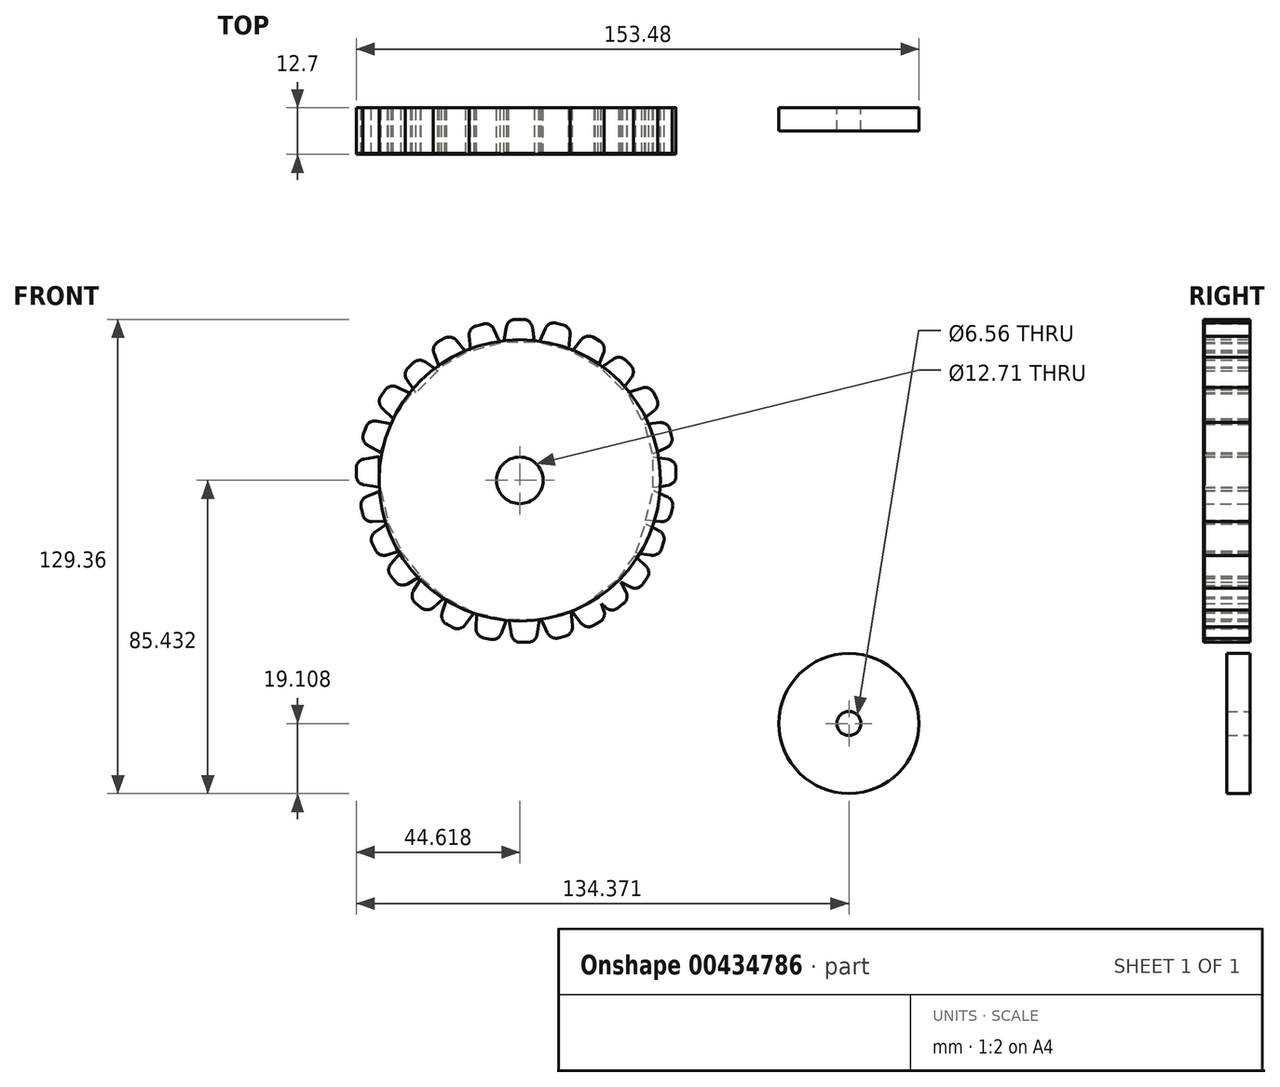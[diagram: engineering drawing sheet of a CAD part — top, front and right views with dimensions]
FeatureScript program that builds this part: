
annotation { "Feature Type Name" : "Feature", "Feature Type Description" : "" }
export const myFeature = defineFeature(function(context is Context, id is Id, definition is map)
    precondition{}
    {
        {
            var Q0;
            Q0=qCreatedBy(makeId("Front.planeOp"),FACE);
            var sketch = newSketch(context, id + "F0", { "sketchPlane" : qUnion([Q0])});
            skCircle(sketch, "E0", {"center": v(-43.7, 42.4) * mm, "radius": 38.36 * mm});
            skCircle(sketch, "E1", {"center": v(-43.7, 42.4) * mm, "radius": 6.36 * mm});
            skSolve(sketch);
        }
        {
            var Q0;
            Q0 = qSketchRegion(id + "F0", true);
            extrude(context, id + "F1", {"entities" : qUnion([Q0]), "depth" : 12.7 * mm});
        }
        {
            var Q0;
            Q0=qCreatedBy(makeId("Front.planeOp"),FACE);
            var sketch = newSketch(context, id + "F2", { "sketchPlane" : qUnion([Q0])});
            skCircle(sketch, "E2", {"center": v(46.06, -23.92) * mm, "radius": 19.1 * mm});
            skCircle(sketch, "E3", {"center": v(46.06, -23.92) * mm, "radius": 3.28 * mm});
            skSolve(sketch);
        }
        {
            var Q0;
            Q0 = qSketchRegion(id + "F2", true);
            extrude(context, id + "F3", {"entities" : qUnion([Q0]), "depth" : 6.35 * mm});
        }
        {
            var Q0;
            Q0=qCreatedBy(makeId("Front.planeOp"),FACE);
            var sketch = newSketch(context, id + "F4", { "sketchPlane" : qUnion([Q0])});
            skLineSegment(sketch, "E4", {"start": v(-44.84, 86.33) * mm, "end": v(-42.81, 86.33) * mm});
            skLineSegment(sketch, "E5", {"start": v(-40.3, 84.2) * mm, "end": v(-39.64, 80.06) * mm});
            skLineSegment(sketch, "E6", {"start": v(-39.64, 80.06) * mm, "end": v(-48.02, 80.06) * mm});
            skLineSegment(sketch, "E7", {"start": v(-48.02, 80.06) * mm, "end": v(-47.35, 84.2) * mm});
            skPoint(sketch, "E8.visualSharp", {"position": v(-40.65, 86.33) * mm});
            skArc(sketch, "E8.filletArc", {"start": v(-40.3, 84.2) * mm, "mid": v(-41.17, 85.73) * mm, "end": v(-42.81, 86.33) * mm});
            skPoint(sketch, "E9.visualSharp", {"position": v(-47, 86.33) * mm});
            skArc(sketch, "E9.filletArc", {"start": v(-44.84, 86.33) * mm, "mid": v(-46.49, 85.73) * mm, "end": v(-47.35, 84.2) * mm});
            skLineSegment(sketch, "E10", {"start": v(-33.75, 85.27) * mm, "end": v(-31.8, 84.75) * mm});
            skLineSegment(sketch, "E11", {"start": v(-29.92, 82.04) * mm, "end": v(-30.34, 77.87) * mm});
            skLineSegment(sketch, "E12", {"start": v(-30.34, 77.87) * mm, "end": v(-38.44, 80.04) * mm});
            skLineSegment(sketch, "E13", {"start": v(-38.44, 80.04) * mm, "end": v(-36.72, 83.86) * mm});
            skPoint(sketch, "E14.visualSharp", {"position": v(-29.7, 84.19) * mm});
            skArc(sketch, "E14.filletArc", {"start": v(-29.92, 82.04) * mm, "mid": v(-30.36, 83.74) * mm, "end": v(-31.8, 84.75) * mm});
            skPoint(sketch, "E15.visualSharp", {"position": v(-35.84, 85.83) * mm});
            skArc(sketch, "E15.filletArc", {"start": v(-33.75, 85.27) * mm, "mid": v(-35.5, 85.11) * mm, "end": v(-36.72, 83.86) * mm});
            skLineSegment(sketch, "E16", {"start": v(-23.67, 81.41) * mm, "end": v(-21.92, 80.4) * mm});
            skLineSegment(sketch, "E17", {"start": v(-20.81, 77.3) * mm, "end": v(-22.3, 73.38) * mm});
            skLineSegment(sketch, "E18", {"start": v(-22.3, 73.38) * mm, "end": v(-29.56, 77.57) * mm});
            skLineSegment(sketch, "E19", {"start": v(-29.56, 77.57) * mm, "end": v(-26.91, 80.82) * mm});
            skPoint(sketch, "E20.visualSharp", {"position": v(-20.04, 79.32) * mm});
            skArc(sketch, "E20.filletArc", {"start": v(-20.81, 77.3) * mm, "mid": v(-20.8, 79.05) * mm, "end": v(-21.92, 80.4) * mm});
            skPoint(sketch, "E21.visualSharp", {"position": v(-25.54, 82.5) * mm});
            skArc(sketch, "E21.filletArc", {"start": v(-23.67, 81.41) * mm, "mid": v(-25.4, 81.7) * mm, "end": v(-26.91, 80.82) * mm});
            skLineSegment(sketch, "E22", {"start": v(-14.9, 75.23) * mm, "end": v(-13.47, 73.8) * mm});
            skLineSegment(sketch, "E23", {"start": v(-13.2, 70.52) * mm, "end": v(-15.66, 67.12) * mm});
            skLineSegment(sketch, "E24", {"start": v(-15.66, 67.12) * mm, "end": v(-21.58, 73.05) * mm});
            skLineSegment(sketch, "E25", {"start": v(-21.58, 73.05) * mm, "end": v(-18.19, 75.5) * mm});
            skPoint(sketch, "E26.visualSharp", {"position": v(-11.94, 72.27) * mm});
            skArc(sketch, "E26.filletArc", {"start": v(-13.2, 70.52) * mm, "mid": v(-12.74, 72.2) * mm, "end": v(-13.47, 73.8) * mm});
            skPoint(sketch, "E27.visualSharp", {"position": v(-16.43, 76.76) * mm});
            skArc(sketch, "E27.filletArc", {"start": v(-14.9, 75.23) * mm, "mid": v(-16.5, 75.97) * mm, "end": v(-18.19, 75.5) * mm});
            skLineSegment(sketch, "E28", {"start": v(-2.77, 56.28) * mm, "end": v(-2.25, 54.33) * mm});
            skLineSegment(sketch, "E29", {"start": v(-3.66, 51.35) * mm, "end": v(-7.48, 49.64) * mm});
            skLineSegment(sketch, "E30", {"start": v(-7.48, 49.64) * mm, "end": v(-9.65, 57.73) * mm});
            skLineSegment(sketch, "E31", {"start": v(-9.65, 57.73) * mm, "end": v(-5.48, 58.15) * mm});
            skPoint(sketch, "E32.visualSharp", {"position": v(-1.69, 52.24) * mm});
            skArc(sketch, "E32.filletArc", {"start": v(-3.66, 51.35) * mm, "mid": v(-2.4, 52.58) * mm, "end": v(-2.25, 54.33) * mm});
            skPoint(sketch, "E33.visualSharp", {"position": v(-3.33, 58.37) * mm});
            skArc(sketch, "E33.filletArc", {"start": v(-2.77, 56.28) * mm, "mid": v(-3.78, 57.72) * mm, "end": v(-5.48, 58.15) * mm});
            skLineSegment(sketch, "E34", {"start": v(-1.08, 45.63) * mm, "end": v(-1.08, 43.6) * mm});
            skLineSegment(sketch, "E35", {"start": v(-3.21, 41.1) * mm, "end": v(-7.35, 40.42) * mm});
            skLineSegment(sketch, "E36", {"start": v(-7.35, 40.42) * mm, "end": v(-7.35, 48.8) * mm});
            skLineSegment(sketch, "E37", {"start": v(-7.35, 48.8) * mm, "end": v(-3.21, 48.13) * mm});
            skPoint(sketch, "E38.visualSharp", {"position": v(-1.08, 41.44) * mm});
            skArc(sketch, "E38.filletArc", {"start": v(-3.21, 41.1) * mm, "mid": v(-1.68, 41.95) * mm, "end": v(-1.08, 43.6) * mm});
            skPoint(sketch, "E39.visualSharp", {"position": v(-1.08, 47.79) * mm});
            skArc(sketch, "E39.filletArc", {"start": v(-1.08, 45.63) * mm, "mid": v(-1.68, 47.27) * mm, "end": v(-3.21, 48.13) * mm});
            skLineSegment(sketch, "E40", {"start": v(-2.04, 34.95) * mm, "end": v(-2.57, 32.99) * mm});
            skLineSegment(sketch, "E41", {"start": v(-5.28, 31.12) * mm, "end": v(-9.45, 31.54) * mm});
            skLineSegment(sketch, "E42", {"start": v(-9.45, 31.54) * mm, "end": v(-7.28, 39.64) * mm});
            skLineSegment(sketch, "E43", {"start": v(-7.28, 39.64) * mm, "end": v(-3.46, 37.92) * mm});
            skPoint(sketch, "E44.visualSharp", {"position": v(-3.13, 30.9) * mm});
            skArc(sketch, "E44.filletArc", {"start": v(-5.28, 31.12) * mm, "mid": v(-3.58, 31.55) * mm, "end": v(-2.57, 32.99) * mm});
            skPoint(sketch, "E45.visualSharp", {"position": v(-1.48, 37.03) * mm});
            skArc(sketch, "E45.filletArc", {"start": v(-2.04, 34.95) * mm, "mid": v(-2.2, 36.7) * mm, "end": v(-3.46, 37.92) * mm});
            skLineSegment(sketch, "E46", {"start": v(-7.3, 66.4) * mm, "end": v(-6.37, 64.6) * mm});
            skLineSegment(sketch, "E47", {"start": v(-7.1, 61.4) * mm, "end": v(-10.47, 58.9) * mm});
            skLineSegment(sketch, "E48", {"start": v(-10.47, 58.9) * mm, "end": v(-14.32, 66.34) * mm});
            skLineSegment(sketch, "E49", {"start": v(-14.32, 66.34) * mm, "end": v(-10.34, 67.65) * mm});
            skPoint(sketch, "E50.visualSharp", {"position": v(-5.37, 62.68) * mm});
            skArc(sketch, "E50.filletArc", {"start": v(-7.1, 61.4) * mm, "mid": v(-6.15, 62.86) * mm, "end": v(-6.37, 64.6) * mm});
            skPoint(sketch, "E51.visualSharp", {"position": v(-8.3, 68.32) * mm});
            skArc(sketch, "E51.filletArc", {"start": v(-7.3, 66.4) * mm, "mid": v(-8.6, 67.59) * mm, "end": v(-10.34, 67.65) * mm});
            skLineSegment(sketch, "E52", {"start": v(-4.45, 25.63) * mm, "end": v(-5.07, 23.7) * mm});
            skLineSegment(sketch, "E53", {"start": v(-7.87, 21.97) * mm, "end": v(-12.01, 22.6) * mm});
            skLineSegment(sketch, "E54", {"start": v(-12.01, 22.6) * mm, "end": v(-9.45, 30.58) * mm});
            skLineSegment(sketch, "E55", {"start": v(-9.45, 30.58) * mm, "end": v(-5.71, 28.67) * mm});
            skPoint(sketch, "E56.visualSharp", {"position": v(-5.74, 21.65) * mm});
            skArc(sketch, "E56.filletArc", {"start": v(-7.87, 21.97) * mm, "mid": v(-6.15, 22.32) * mm, "end": v(-5.07, 23.7) * mm});
            skPoint(sketch, "E57.visualSharp", {"position": v(-3.79, 27.7) * mm});
            skArc(sketch, "E57.filletArc", {"start": v(-4.45, 25.63) * mm, "mid": v(-4.52, 27.39) * mm, "end": v(-5.71, 28.67) * mm});
            skLineSegment(sketch, "E58", {"start": v(-55.67, 84.5) * mm, "end": v(-53.71, 85.02) * mm});
            skLineSegment(sketch, "E59", {"start": v(-50.74, 83.61) * mm, "end": v(-49.02, 79.8) * mm});
            skLineSegment(sketch, "E60", {"start": v(-49.02, 79.8) * mm, "end": v(-57.12, 77.62) * mm});
            skLineSegment(sketch, "E61", {"start": v(-57.12, 77.62) * mm, "end": v(-57.54, 81.79) * mm});
            skPoint(sketch, "E62.visualSharp", {"position": v(-51.62, 85.58) * mm});
            skArc(sketch, "E62.filletArc", {"start": v(-50.74, 83.61) * mm, "mid": v(-51.97, 84.86) * mm, "end": v(-53.71, 85.02) * mm});
            skPoint(sketch, "E63.visualSharp", {"position": v(-57.76, 83.94) * mm});
            skArc(sketch, "E63.filletArc", {"start": v(-55.67, 84.5) * mm, "mid": v(-57.1, 83.49) * mm, "end": v(-57.54, 81.79) * mm});
            skLineSegment(sketch, "E64", {"start": v(-66, 80.13) * mm, "end": v(-64.24, 81.15) * mm});
            skLineSegment(sketch, "E65", {"start": v(-61, 80.55) * mm, "end": v(-58.36, 77.3) * mm});
            skLineSegment(sketch, "E66", {"start": v(-58.36, 77.3) * mm, "end": v(-65.62, 73.12) * mm});
            skLineSegment(sketch, "E67", {"start": v(-65.62, 73.12) * mm, "end": v(-67.1, 77.03) * mm});
            skPoint(sketch, "E68.visualSharp", {"position": v(-62.37, 82.23) * mm});
            skArc(sketch, "E68.filletArc", {"start": v(-61, 80.55) * mm, "mid": v(-62.52, 81.45) * mm, "end": v(-64.24, 81.15) * mm});
            skPoint(sketch, "E69.visualSharp", {"position": v(-67.87, 79.05) * mm});
            skArc(sketch, "E69.filletArc", {"start": v(-66, 80.13) * mm, "mid": v(-67.12, 78.79) * mm, "end": v(-67.1, 77.03) * mm});
            skLineSegment(sketch, "E70", {"start": v(-74.2, 73.01) * mm, "end": v(-72.76, 74.45) * mm});
            skLineSegment(sketch, "E71", {"start": v(-69.48, 74.71) * mm, "end": v(-66.08, 72.26) * mm});
            skLineSegment(sketch, "E72", {"start": v(-66.08, 72.26) * mm, "end": v(-72.01, 66.33) * mm});
            skLineSegment(sketch, "E73", {"start": v(-72.01, 66.33) * mm, "end": v(-74.46, 69.73) * mm});
            skPoint(sketch, "E74.visualSharp", {"position": v(-71.23, 75.97) * mm});
            skArc(sketch, "E74.filletArc", {"start": v(-69.48, 74.71) * mm, "mid": v(-71.17, 75.18) * mm, "end": v(-72.76, 74.45) * mm});
            skPoint(sketch, "E75.visualSharp", {"position": v(-75.72, 71.48) * mm});
            skArc(sketch, "E75.filletArc", {"start": v(-74.2, 73.01) * mm, "mid": v(-74.93, 71.42) * mm, "end": v(-74.46, 69.73) * mm});
            skLineSegment(sketch, "E76", {"start": v(-81.56, 65.4) * mm, "end": v(-80.4, 67.06) * mm});
            skLineSegment(sketch, "E77", {"start": v(-77.2, 67.9) * mm, "end": v(-73.44, 66.07) * mm});
            skLineSegment(sketch, "E78", {"start": v(-73.44, 66.07) * mm, "end": v(-78.24, 59.2) * mm});
            skLineSegment(sketch, "E79", {"start": v(-78.24, 59.2) * mm, "end": v(-81.25, 62.13) * mm});
            skArc(sketch, "E80.filletArc", {"start": v(-77.2, 67.9) * mm, "mid": v(-78.95, 68.07) * mm, "end": v(-80.4, 67.06) * mm});
            skArc(sketch, "E81.filletArc", {"start": v(-81.56, 65.4) * mm, "mid": v(-82, 63.7) * mm, "end": v(-81.25, 62.13) * mm});
            skLineSegment(sketch, "E82", {"start": v(-86.34, 55.05) * mm, "end": v(-85.64, 56.95) * mm});
            skLineSegment(sketch, "E83", {"start": v(-82.78, 58.58) * mm, "end": v(-78.67, 57.8) * mm});
            skLineSegment(sketch, "E84", {"start": v(-78.67, 57.8) * mm, "end": v(-81.53, 49.92) * mm});
            skLineSegment(sketch, "E85", {"start": v(-81.53, 49.92) * mm, "end": v(-85.2, 51.96) * mm});
            skPoint(sketch, "E86.visualSharp", {"position": v(-84.9, 58.98) * mm});
            skArc(sketch, "E86.filletArc", {"start": v(-82.78, 58.58) * mm, "mid": v(-84.51, 58.29) * mm, "end": v(-85.64, 56.95) * mm});
            skPoint(sketch, "E87.visualSharp", {"position": v(-87.08, 53.01) * mm});
            skArc(sketch, "E87.filletArc", {"start": v(-86.34, 55.05) * mm, "mid": v(-86.33, 53.3) * mm, "end": v(-85.2, 51.96) * mm});
            skLineSegment(sketch, "E88", {"start": v(-88.3, 43.7) * mm, "end": v(-88.3, 45.73) * mm});
            skLineSegment(sketch, "E89", {"start": v(-86.17, 48.24) * mm, "end": v(-82.04, 48.9) * mm});
            skLineSegment(sketch, "E90", {"start": v(-82.04, 48.9) * mm, "end": v(-82.04, 40.52) * mm});
            skLineSegment(sketch, "E91", {"start": v(-82.04, 40.52) * mm, "end": v(-86.17, 41.2) * mm});
            skArc(sketch, "E92.filletArc", {"start": v(-86.17, 48.24) * mm, "mid": v(-87.7, 47.37) * mm, "end": v(-88.3, 45.73) * mm});
            skArc(sketch, "E93.filletArc", {"start": v(-88.3, 43.7) * mm, "mid": v(-87.7, 42.05) * mm, "end": v(-86.17, 41.2) * mm});
            skLineSegment(sketch, "E94", {"start": v(-86.54, 33.1) * mm, "end": v(-86.98, 35.08) * mm});
            skLineSegment(sketch, "E95", {"start": v(-85.44, 37.99) * mm, "end": v(-81.55, 39.54) * mm});
            skLineSegment(sketch, "E96", {"start": v(-81.55, 39.54) * mm, "end": v(-79.73, 31.36) * mm});
            skLineSegment(sketch, "E97", {"start": v(-79.73, 31.36) * mm, "end": v(-83.91, 31.11) * mm});
            skPoint(sketch, "E98.visualSharp", {"position": v(-87.45, 37.19) * mm});
            skArc(sketch, "E98.filletArc", {"start": v(-85.44, 37.99) * mm, "mid": v(-86.75, 36.82) * mm, "end": v(-86.98, 35.08) * mm});
            skPoint(sketch, "E99.visualSharp", {"position": v(-86.07, 30.99) * mm});
            skArc(sketch, "E99.filletArc", {"start": v(-86.54, 33.1) * mm, "mid": v(-85.6, 31.62) * mm, "end": v(-83.91, 31.11) * mm});
            skLineSegment(sketch, "E100", {"start": v(-83.05, 23.35) * mm, "end": v(-83.93, 25.18) * mm});
            skLineSegment(sketch, "E101", {"start": v(-83.1, 28.36) * mm, "end": v(-79.67, 30.77) * mm});
            skLineSegment(sketch, "E102", {"start": v(-79.67, 30.77) * mm, "end": v(-76.02, 23.22) * mm});
            skLineSegment(sketch, "E103", {"start": v(-76.02, 23.22) * mm, "end": v(-80.04, 22.02) * mm});
            skPoint(sketch, "E104.visualSharp", {"position": v(-84.87, 27.13) * mm});
            skArc(sketch, "E104.filletArc", {"start": v(-83.1, 28.36) * mm, "mid": v(-84.1, 26.93) * mm, "end": v(-83.93, 25.18) * mm});
            skPoint(sketch, "E105.visualSharp", {"position": v(-82.1, 21.4) * mm});
            skArc(sketch, "E105.filletArc", {"start": v(-83.05, 23.35) * mm, "mid": v(-81.79, 22.13) * mm, "end": v(-80.04, 22.02) * mm});
            skLineSegment(sketch, "E106", {"start": v(-77.59, 14.74) * mm, "end": v(-78.87, 16.31) * mm});
            skLineSegment(sketch, "E107", {"start": v(-78.81, 19.6) * mm, "end": v(-76.04, 22.74) * mm});
            skLineSegment(sketch, "E108", {"start": v(-76.04, 22.74) * mm, "end": v(-70.73, 16.26) * mm});
            skLineSegment(sketch, "E109", {"start": v(-70.73, 16.26) * mm, "end": v(-74.35, 14.15) * mm});
            skPoint(sketch, "E110.visualSharp", {"position": v(-80.24, 17.98) * mm});
            skArc(sketch, "E110.filletArc", {"start": v(-78.81, 19.6) * mm, "mid": v(-79.45, 17.97) * mm, "end": v(-78.87, 16.31) * mm});
            skPoint(sketch, "E111.visualSharp", {"position": v(-76.22, 13.07) * mm});
            skArc(sketch, "E111.filletArc", {"start": v(-77.59, 14.74) * mm, "mid": v(-76.08, 13.85) * mm, "end": v(-74.35, 14.15) * mm});
            skLineSegment(sketch, "E112", {"start": v(-70.61, 7.69) * mm, "end": v(-72.17, 8.99) * mm});
            skLineSegment(sketch, "E113", {"start": v(-72.72, 12.23) * mm, "end": v(-70.57, 15.83) * mm});
            skLineSegment(sketch, "E114", {"start": v(-70.57, 15.83) * mm, "end": v(-64.15, 10.44) * mm});
            skLineSegment(sketch, "E115", {"start": v(-64.15, 10.44) * mm, "end": v(-67.32, 7.7) * mm});
            skPoint(sketch, "E116.visualSharp", {"position": v(-73.82, 10.38) * mm});
            skArc(sketch, "E116.filletArc", {"start": v(-72.72, 12.23) * mm, "mid": v(-73.04, 10.51) * mm, "end": v(-72.17, 8.99) * mm});
            skPoint(sketch, "E117.visualSharp", {"position": v(-68.96, 6.3) * mm});
            skArc(sketch, "E117.filletArc", {"start": v(-70.61, 7.69) * mm, "mid": v(-68.96, 7.1) * mm, "end": v(-67.32, 7.7) * mm});
            skLineSegment(sketch, "E118", {"start": v(-61.83, 2.22) * mm, "end": v(-63.63, 3.16) * mm});
            skLineSegment(sketch, "E119", {"start": v(-64.88, 6.2) * mm, "end": v(-63.57, 10.19) * mm});
            skLineSegment(sketch, "E120", {"start": v(-63.57, 10.19) * mm, "end": v(-56.13, 6.33) * mm});
            skLineSegment(sketch, "E121", {"start": v(-56.13, 6.33) * mm, "end": v(-58.62, 2.96) * mm});
            skPoint(sketch, "E122.visualSharp", {"position": v(-65.55, 4.15) * mm});
            skArc(sketch, "E122.filletArc", {"start": v(-64.88, 6.2) * mm, "mid": v(-64.81, 4.45) * mm, "end": v(-63.63, 3.16) * mm});
            skPoint(sketch, "E123.visualSharp", {"position": v(-59.91, 1.23) * mm});
            skArc(sketch, "E123.filletArc", {"start": v(-61.83, 2.22) * mm, "mid": v(-60.1, 2) * mm, "end": v(-58.62, 2.96) * mm});
            skLineSegment(sketch, "E124", {"start": v(-9, 15.74) * mm, "end": v(-10.15, 14.08) * mm});
            skLineSegment(sketch, "E125", {"start": v(-13.34, 13.25) * mm, "end": v(-17.11, 15.07) * mm});
            skLineSegment(sketch, "E126", {"start": v(-17.11, 15.07) * mm, "end": v(-12.3, 21.94) * mm});
            skLineSegment(sketch, "E127", {"start": v(-12.3, 21.94) * mm, "end": v(-9.3, 19.02) * mm});
            skPoint(sketch, "E128.visualSharp", {"position": v(-11.4, 12.31) * mm});
            skArc(sketch, "E128.filletArc", {"start": v(-13.34, 13.25) * mm, "mid": v(-11.6, 13.08) * mm, "end": v(-10.15, 14.08) * mm});
            skPoint(sketch, "E129.visualSharp", {"position": v(-7.75, 17.51) * mm});
            skArc(sketch, "E129.filletArc", {"start": v(-9, 15.74) * mm, "mid": v(-8.54, 17.44) * mm, "end": v(-9.3, 19.02) * mm});
            skLineSegment(sketch, "E130", {"start": v(-51.66, -0.96) * mm, "end": v(-53.65, -0.53) * mm});
            skLineSegment(sketch, "E131", {"start": v(-55.65, 2.08) * mm, "end": v(-55.43, 6.26) * mm});
            skLineSegment(sketch, "E132", {"start": v(-55.43, 6.26) * mm, "end": v(-47.24, 4.5) * mm});
            skLineSegment(sketch, "E133", {"start": v(-47.24, 4.5) * mm, "end": v(-48.76, 0.6) * mm});
            skPoint(sketch, "E134.visualSharp", {"position": v(-55.76, -0.08) * mm});
            skArc(sketch, "E134.filletArc", {"start": v(-55.65, 2.08) * mm, "mid": v(-55.13, 0.4) * mm, "end": v(-53.65, -0.53) * mm});
            skPoint(sketch, "E135.visualSharp", {"position": v(-49.55, -1.41) * mm});
            skArc(sketch, "E135.filletArc", {"start": v(-51.66, -0.96) * mm, "mid": v(-49.93, -0.71) * mm, "end": v(-48.76, 0.6) * mm});
            skLineSegment(sketch, "E136", {"start": v(-41.48, -1.79) * mm, "end": v(-43.5, -1.79) * mm});
            skLineSegment(sketch, "E137", {"start": v(-46.01, 0.35) * mm, "end": v(-46.68, 4.48) * mm});
            skLineSegment(sketch, "E138", {"start": v(-46.68, 4.48) * mm, "end": v(-38.3, 4.48) * mm});
            skLineSegment(sketch, "E139", {"start": v(-38.3, 4.48) * mm, "end": v(-38.97, 0.35) * mm});
            skPoint(sketch, "E140.visualSharp", {"position": v(-45.67, -1.79) * mm});
            skArc(sketch, "E140.filletArc", {"start": v(-46.01, 0.35) * mm, "mid": v(-45.15, -1.18) * mm, "end": v(-43.5, -1.79) * mm});
            skPoint(sketch, "E141.visualSharp", {"position": v(-39.32, -1.79) * mm});
            skArc(sketch, "E141.filletArc", {"start": v(-41.48, -1.79) * mm, "mid": v(-39.83, -1.18) * mm, "end": v(-38.97, 0.35) * mm});
            skLineSegment(sketch, "E142", {"start": v(-31.21, -0.06) * mm, "end": v(-33.17, -0.58) * mm});
            skLineSegment(sketch, "E143", {"start": v(-36.14, 0.83) * mm, "end": v(-37.86, 4.65) * mm});
            skLineSegment(sketch, "E144", {"start": v(-37.86, 4.65) * mm, "end": v(-29.76, 6.82) * mm});
            skLineSegment(sketch, "E145", {"start": v(-29.76, 6.82) * mm, "end": v(-29.34, 2.65) * mm});
            skPoint(sketch, "E146.visualSharp", {"position": v(-35.26, -1.14) * mm});
            skArc(sketch, "E146.filletArc", {"start": v(-36.14, 0.83) * mm, "mid": v(-34.92, -0.42) * mm, "end": v(-33.17, -0.58) * mm});
            skPoint(sketch, "E147.visualSharp", {"position": v(-29.12, 0.5) * mm});
            skArc(sketch, "E147.filletArc", {"start": v(-31.21, -0.06) * mm, "mid": v(-29.78, 0.95) * mm, "end": v(-29.34, 2.65) * mm});
            skLineSegment(sketch, "E148", {"start": v(-21.88, 3.8) * mm, "end": v(-23.63, 2.78) * mm});
            skLineSegment(sketch, "E149", {"start": v(-26.87, 3.38) * mm, "end": v(-29.52, 6.62) * mm});
            skLineSegment(sketch, "E150", {"start": v(-29.52, 6.62) * mm, "end": v(-22.26, 10.81) * mm});
            skLineSegment(sketch, "E151", {"start": v(-22.26, 10.81) * mm, "end": v(-20.77, 6.9) * mm});
            skPoint(sketch, "E152.visualSharp", {"position": v(-25.5, 1.7) * mm});
            skArc(sketch, "E152.filletArc", {"start": v(-26.87, 3.38) * mm, "mid": v(-25.36, 2.48) * mm, "end": v(-23.63, 2.78) * mm});
            skPoint(sketch, "E153.visualSharp", {"position": v(-20, 4.88) * mm});
            skArc(sketch, "E153.filletArc", {"start": v(-21.88, 3.8) * mm, "mid": v(-20.76, 5.14) * mm, "end": v(-20.77, 6.9) * mm});
            skLineSegment(sketch, "E154", {"start": v(-15.45, 8.76) * mm, "end": v(-17.07, 7.53) * mm});
            skLineSegment(sketch, "E155", {"start": v(-20.35, 7.73) * mm, "end": v(-23.38, 10.62) * mm});
            skLineSegment(sketch, "E156", {"start": v(-23.38, 10.62) * mm, "end": v(-16.7, 15.67) * mm});
            skLineSegment(sketch, "E157", {"start": v(-16.7, 15.67) * mm, "end": v(-14.73, 11.97) * mm});
            skPoint(sketch, "E158.visualSharp", {"position": v(-18.8, 6.23) * mm});
            skArc(sketch, "E158.filletArc", {"start": v(-20.35, 7.73) * mm, "mid": v(-18.74, 7.03) * mm, "end": v(-17.07, 7.53) * mm});
            skPoint(sketch, "E159.visualSharp", {"position": v(-13.72, 10.06) * mm});
            skArc(sketch, "E159.filletArc", {"start": v(-15.45, 8.76) * mm, "mid": v(-14.5, 10.23) * mm, "end": v(-14.73, 11.97) * mm});
            skSolve(sketch);
        }
        {
            var Q0;
            Q0 = qSketchRegion(id + "F4", true);
            extrude(context, id + "F5", {"entities" : qUnion([Q0]), "depth" : 12.62 * mm});
        }
        {
            var Q0;
            Q0 = qSketchRegion(id + "F4", true);
            extrude(context, id + "F6", {"entities" : qUnion([Q0]), "depth" : 12.45 * mm});
        }
    });
